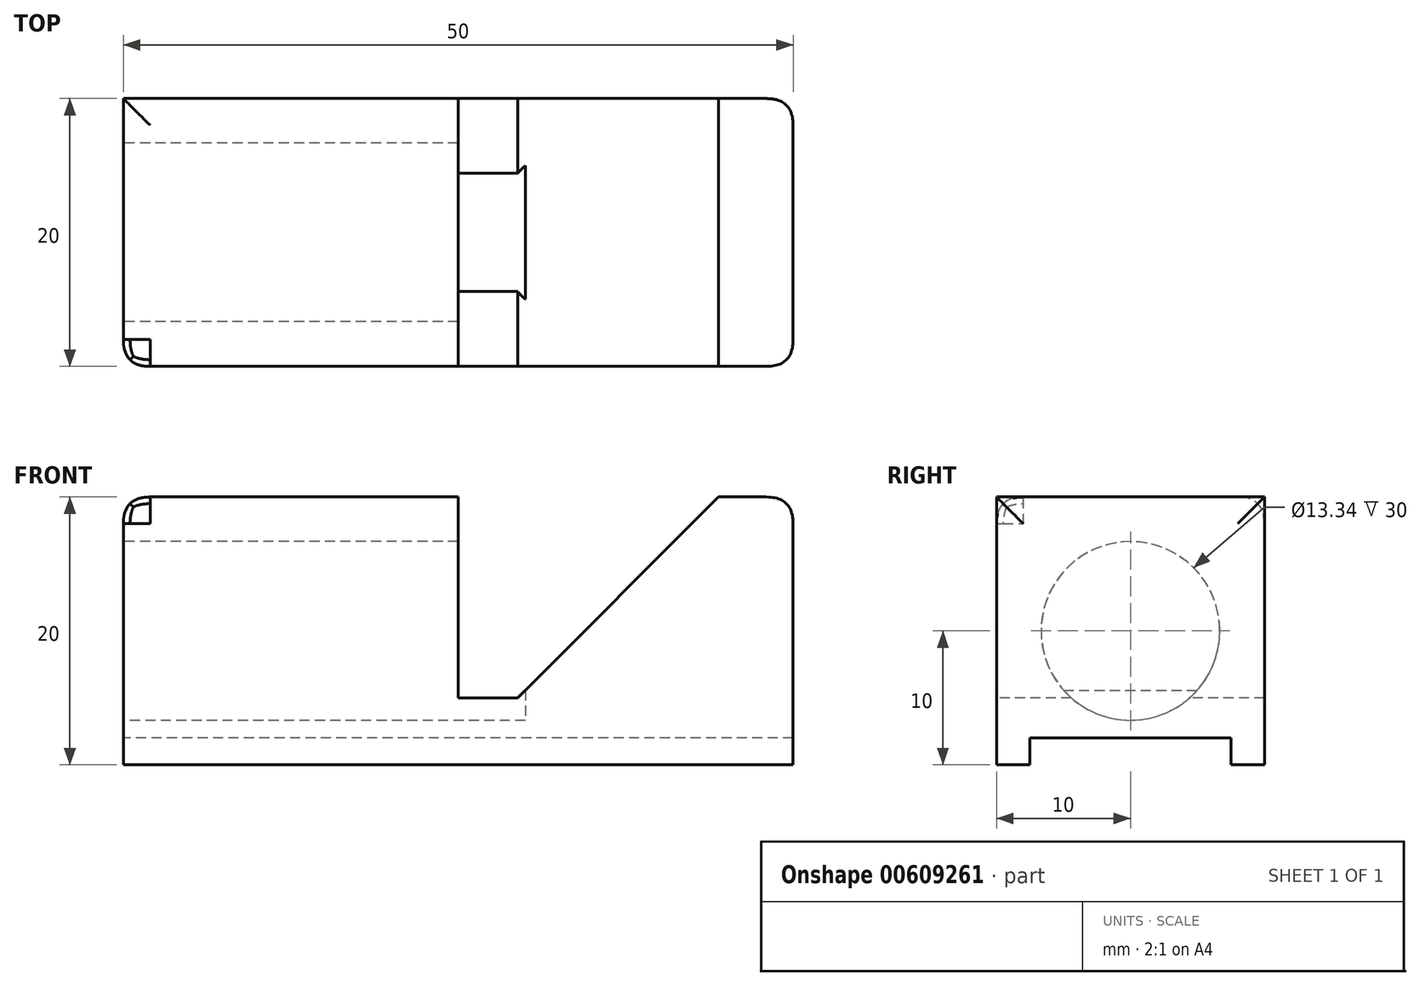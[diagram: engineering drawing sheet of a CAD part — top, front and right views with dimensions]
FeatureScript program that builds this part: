
annotation { "Feature Type Name" : "Feature", "Feature Type Description" : "" }
export const myFeature = defineFeature(function(context is Context, id is Id, definition is map)
    precondition{}
    {
        {
            var Q0;
            Q0=qCreatedBy(makeId("Top.planeOp"),FACE);
            var sketch = newSketch(context, id + "F0", { "sketchPlane" : qUnion([Q0])});
            skLineSegment(sketch, "E0.bottom", {"start": v(-16.47, 10) * mm, "end": v(33.53, 10) * mm});
            skLineSegment(sketch, "E0.top", {"start": v(-16.47, -10) * mm, "end": v(33.53, -10) * mm});
            skLineSegment(sketch, "E0.left", {"start": v(-16.47, 10) * mm, "end": v(-16.47, -10) * mm});
            skLineSegment(sketch, "E0.right", {"start": v(33.53, 10) * mm, "end": v(33.53, -10) * mm});
            skLineSegment(sketch, "E1", {"start": v(-3.55, -10) * mm, "end": v(-3.55, 0) * mm});
            skLineSegment(sketch, "E2", {"start": v(-3.55, 0) * mm, "end": v(-3.55, 10) * mm});
            skPoint(sketch, "E2.endSnap0", {"position": v(8.53, 10) * mm});
            skSolve(sketch);
        }
        {
            var Q0;
            Q0 = qSketchRegion(id + "F0", true);
            extrude(context, id + "F1", {"entities" : qUnion([Q0]), "depth" : 20 * mm, "offsetDistance" : 25.4 * mm});
        }
        {
            var Q0;
            Q0=makeQuery(id+"F1.opExtrude","SWEPT_FACE",FACE,{"disambiguationData":[OSD([sQuery(id+"F0.wireOp",EDGE,"E0.top")])]});
            var sketch = newSketch(context, id + "F2", { "sketchPlane" : qUnion([Q0])});
            skLineSegment(sketch, "E3", {"start": v(8.53, 20) * mm, "end": v(8.53, 5) * mm});
            skLineSegment(sketch, "E4", {"start": v(8.53, 5) * mm, "end": v(12.96, 5) * mm});
            skLineSegment(sketch, "E5", {"start": v(12.96, 5) * mm, "end": v(27.96, 20) * mm});
            skSolve(sketch);
        }
        {
            var Q0;
            Q0 = qSketchRegion(id + "F2", true);
            var Q1;
            {var subQ3=sQuery(id+"F2.wireOp",EDGE,"E3");Q1=makeQuery(id+"F2.imprint","IMPRINT",FACE,{"disambiguationData":[TD([[makeQuery(id+"F2.imprint","IMPRINT",EDGE,{"derivedFrom":subQ3}),-1.0]])]});}
            extrude(context, id + "F3", {"entities" : qUnion([Q0, Q1]), "operationType" : NewBodyOperationType.INTERSECT, "oppositeDirection" : true, "depth" : 508 * mm, "offsetDistance" : 25.4 * mm});
        }
        {
            var Q0;
            Q0=makeQuery(id+"F1.opExtrude","SWEPT_FACE",FACE,{"disambiguationData":[OSD([sQuery(id+"F0.wireOp",EDGE,"E0.left")])]});
            var sketch = newSketch(context, id + "F4", { "sketchPlane" : qUnion([Q0])});
            skCircle(sketch, "E6", {"center": v(0, 10) * mm, "radius": 6.67 * mm});
            skSolve(sketch);
        }
        {
            var Q0;
            Q0=makeQuery(id+"F4.imprint","IMPRINT",FACE,{"disambiguationData":[TD([[makeQuery(id+"F4.imprint","IMPRINT",EDGE,{"derivedFrom":sQuery(id+"F4.wireOp",EDGE,"E6")}),1.0]])]});
            extrude(context, id + "F5", {"entities" : qUnion([Q0]), "operationType" : NewBodyOperationType.REMOVE, "oppositeDirection" : true, "depth" : 30 * mm, "offsetDistance" : 25.4 * mm});
        }
        {
            var Q0;
            Q0=makeQuery(id+"F1.opExtrude","CAP_FACE",FACE,{"disambiguationData":[OSD([sQuery(id+"F0.wireOp",EDGE,"E0.bottom"),sQuery(id+"F0.wireOp",EDGE,"E0.top"),sQuery(id+"F0.wireOp",EDGE,"E0.left"),sQuery(id+"F0.wireOp",EDGE,"E0.right")])],"isStart":true});
            var sketch = newSketch(context, id + "F6", { "sketchPlane" : qUnion([Q0])});
            skLineSegment(sketch, "E7.bottom", {"start": v(36.99, 7.5) * mm, "end": v(-36.99, 7.5) * mm});
            skLineSegment(sketch, "E7.top", {"start": v(36.99, -7.5) * mm, "end": v(-36.99, -7.5) * mm});
            skLineSegment(sketch, "E7.left", {"start": v(36.99, 7.5) * mm, "end": v(36.99, -7.5) * mm});
            skLineSegment(sketch, "E7.right", {"start": v(-36.99, 7.5) * mm, "end": v(-36.99, -7.5) * mm});
            skPoint(sketch, "E7.middle", {"position": v(0, 0) * mm});
            skSolve(sketch);
        }
        {
            var Q0;
            Q0 = qSketchRegion(id + "F6", true);
            extrude(context, id + "F7", {"entities" : qUnion([Q0]), "operationType" : NewBodyOperationType.REMOVE, "oppositeDirection" : true, "depth" : 2 * mm, "offsetDistance" : 25.4 * mm});
        }
        {
            var Q0;
            {var subQ0=sQuery(id+"F0.wireOp",EDGE,"E0.left");var subQ1=sQuery(id+"F0.wireOp",EDGE,"E0.top");Q0=makeQuery(id+"F3.boolean.opBoolean","SPLIT",EDGE,{"disambiguationData":[TD([makeQuery(id+"F1.opExtrude","SWEPT_FACE",FACE,{"disambiguationData":[OSD([subQ0])]})])],"derivedFrom":makeQuery(id+"F1.opExtrude","CAP_EDGE",EDGE,{"disambiguationData":[OSD([subQ1])],"isStart":false})});}
            var Q1;
            Q1=makeQuery(id+"F1.opExtrude","CAP_EDGE",EDGE,{"disambiguationData":[OSD([sQuery(id+"F0.wireOp",EDGE,"E0.left")])],"isStart":false});
            var Q2;
            {var subQ0=sQuery(id+"F0.wireOp",EDGE,"E0.bottom");var subQ1=sQuery(id+"F0.wireOp",EDGE,"E0.left");Q2=makeQuery(id+"F3.boolean.opBoolean","SPLIT",EDGE,{"disambiguationData":[TD([makeQuery(id+"F1.opExtrude","SWEPT_FACE",FACE,{"disambiguationData":[OSD([subQ1])]})])],"derivedFrom":makeQuery(id+"F1.opExtrude","CAP_EDGE",EDGE,{"disambiguationData":[OSD([subQ0])],"isStart":false})});}
            var Q3;
            Q3=makeQuery(id+"F1.opExtrude","SWEPT_EDGE",EDGE,{"disambiguationData":[OSD([sQuery(id+"F0.wireOp",EDGE,"E0.top"),sQuery(id+"F0.wireOp",EDGE,"E0.left")])]});
            var Q4;
            Q4=makeQuery(id+"F1.opExtrude","SWEPT_EDGE",EDGE,{"disambiguationData":[OSD([sQuery(id+"F0.wireOp",EDGE,"E0.top"),sQuery(id+"F0.wireOp",EDGE,"E0.right")])]});
            var Q5;
            Q5=makeQuery(id+"F1.opExtrude","SWEPT_EDGE",EDGE,{"disambiguationData":[OSD([sQuery(id+"F0.wireOp",EDGE,"E0.bottom"),sQuery(id+"F0.wireOp",EDGE,"E0.right")])]});
            var Q6;
            Q6=makeQuery(id+"F1.opExtrude","CAP_EDGE",EDGE,{"disambiguationData":[OSD([sQuery(id+"F0.wireOp",EDGE,"E0.right")])],"isStart":false});
            var Q7;
            Q7=makeQuery(id+"F3.boolean.opBoolean","COPY",EDGE,{"derivedFrom":makeQuery(id+"F3.boolean.toolComplement.opBoolean","COPY",EDGE,{"derivedFrom":makeQuery(id+"F3.opExtrude","SWEPT_EDGE",EDGE,{"disambiguationData":[OSD([sQuery(id+"F0.wireOp",EDGE,"E0.top"),sQuery(id+"F2.wireOp",EDGE,"E3")])]})})});
            fillet(context, id + "F8", {"entities" : qUnion([Q0, Q1, Q2, Q3, Q4, Q5, Q6, Q7]), "radius" : 2 * mm, "tangentPropagation" : true, "rho" : 0.5, "crossSection" : FilletCrossSection.CONIC, "allowEdgeOverflow" : false});
        }
    });
